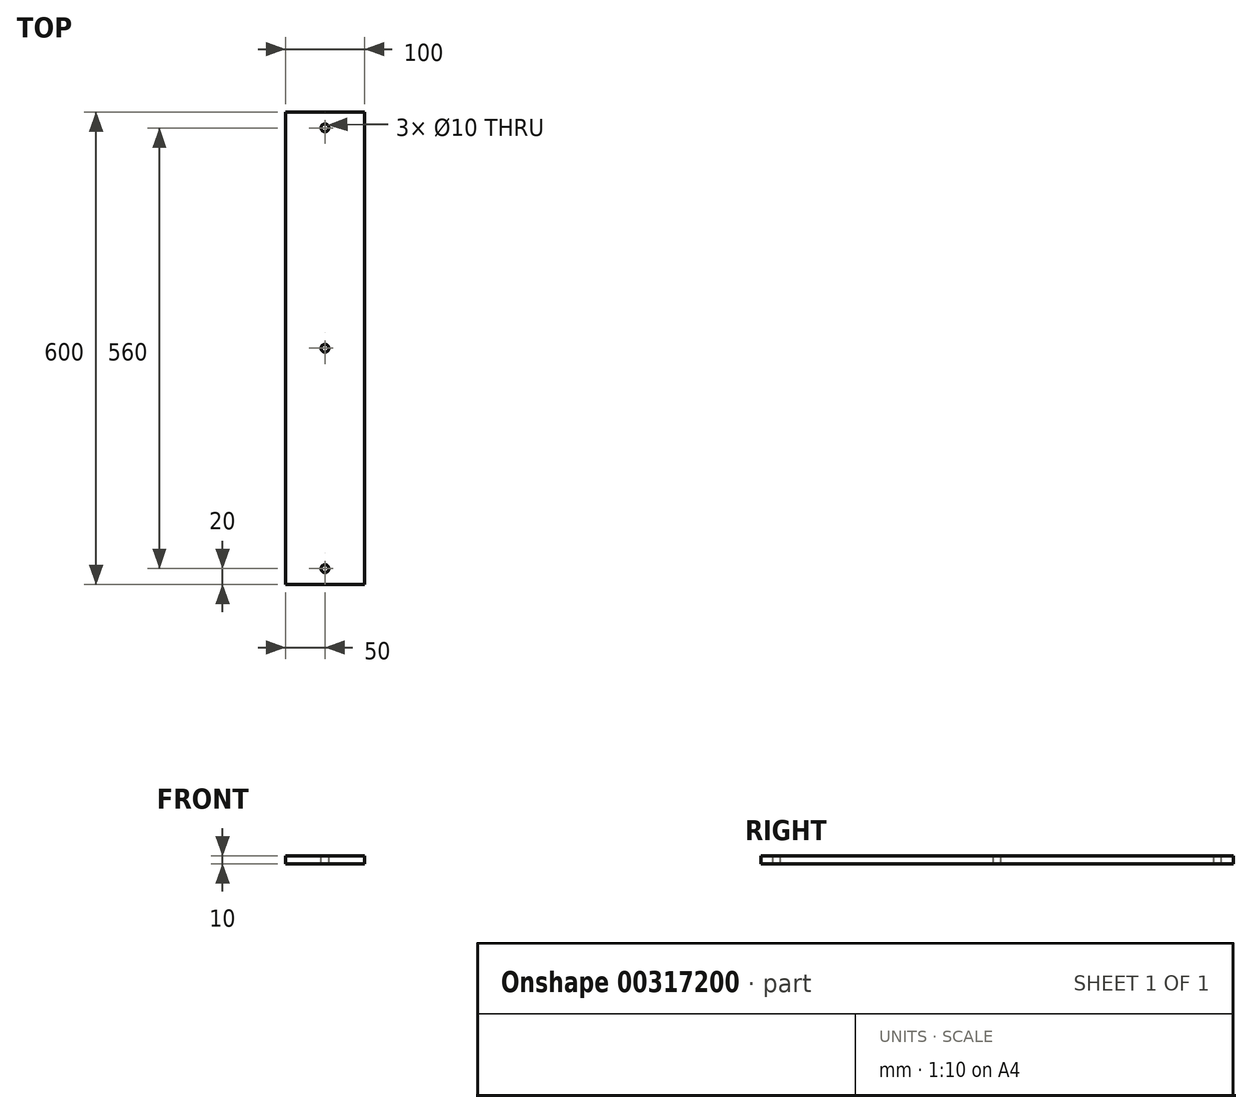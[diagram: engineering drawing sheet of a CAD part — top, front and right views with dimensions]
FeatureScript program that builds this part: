
annotation { "Feature Type Name" : "Feature", "Feature Type Description" : "" }
export const myFeature = defineFeature(function(context is Context, id is Id, definition is map)
    precondition{}
    {
        {
            var Q0;
            Q0=qCreatedBy(makeId("Top.planeOp"),FACE);
            var sketch = newSketch(context, id + "F0", { "sketchPlane" : qUnion([Q0])});
            skLineSegment(sketch, "E0.bottom", {"start": v(-50, 300) * mm, "end": v(50, 300) * mm});
            skLineSegment(sketch, "E0.top", {"start": v(-50, -300) * mm, "end": v(50, -300) * mm});
            skLineSegment(sketch, "E0.left", {"start": v(-50, 300) * mm, "end": v(-50, -300) * mm});
            skLineSegment(sketch, "E0.right", {"start": v(50, 300) * mm, "end": v(50, -300) * mm});
            skLineSegment(sketch, "E1", {"start": v(50, 300) * mm, "end": v(-50, -300) * mm, "construction": true});
            skSolve(sketch);
        }
        {
            var Q0;
            Q0 = qSketchRegion(id + "F0", true);
            extrude(context, id + "F1", {"entities" : qUnion([Q0]), "depth" : 10 * mm});
        }
        {
            var Q0;
            Q0=makeQuery(id+"F1.opExtrude","CAP_FACE",FACE,{"disambiguationData":[OSD([sQuery(id+"F0.wireOp",EDGE,"E0.bottom"),sQuery(id+"F0.wireOp",EDGE,"E0.top"),sQuery(id+"F0.wireOp",EDGE,"E0.left"),sQuery(id+"F0.wireOp",EDGE,"E0.right")])],"isStart":false});
            var sketch = newSketch(context, id + "F2", { "sketchPlane" : qUnion([Q0])});
            skCircle(sketch, "E2", {"center": v(0, 280) * mm, "radius": 5 * mm});
            skCircle(sketch, "E3", {"center": v(0, 0) * mm, "radius": 5 * mm});
            skCircle(sketch, "E4", {"center": v(0, -280) * mm, "radius": 5 * mm});
            skLineSegment(sketch, "E5", {"start": v(0, 280) * mm, "end": v(0, 0) * mm, "construction": true});
            skLineSegment(sketch, "E6", {"start": v(0, -280) * mm, "end": v(0, 0) * mm, "construction": true});
            skSolve(sketch);
        }
        {
            var Q0;
            Q0 = qSketchRegion(id + "F2", true);
            extrude(context, id + "F3", {"entities" : qUnion([Q0]), "operationType" : NewBodyOperationType.REMOVE, "oppositeDirection" : true, "depth" : 25 * mm});
        }
    });
